# Revit family: Magnuson-Oxi_Bistrot-Round_Table-1
name_source: partatom
category: Furniture
revit_build: Autodesk Revit 2016 (Build: 20150220_1215(x64)
units: mm (PartAtom-declared; Revit-internal decimal feet)

## family parameters
Always vertical = Yes
Cut with Voids When Loaded = No
OmniClass Number = 23.40.20.00
OmniClass Title = General Furniture and Specialties
Room Calculation Point = No
Shared = No
Work Plane-Based = No

## types (3) — shared parameters
Assembly Code = E2020200
Base Finish = MAG-Metal Paint Black
Edge Finish = MAG-Phenolic
Glide Finish = MAG-Plastic Black
Keynote = 12500
Leg Finish = MAG-Metal Paint Black
Low Emitting Finish = Yes
Low Emitting Material = Yes
Manufacturer = Magnuson Group
Revit File Built By = https://servex-us.com
Salvage or Reuse = No
Support Finish = MAG-Metal Paint Black
Top Finish = MAG-Phenolic
Type Comments = Outdoor Tables
URL = www.magnusongroup.com
zero-valued in all types: Percentage of Recycled Content

## per-type parameters (varying)
| type | Description | Diameter | Height |
| OXI-10 | Outdoor Table Round  23 5/8"D x 29 1/8"H | 23 5/8" | 29 1/8" |
| OXI-20 | Outdoor Table Round  31 1/2"D x 29 1/8"H | 31 1/2" | 29 1/8" |
| OXI-40 | Outdoor Table Round  23 5/8"D x 43 3/8"H | 23 5/8" | 43 3/8" |

note: column(s) folded — value = type name in every type: Model

## geometry (parser evidence)
native form markers: Sweep x5
no freeform markers — native parametric forms only
